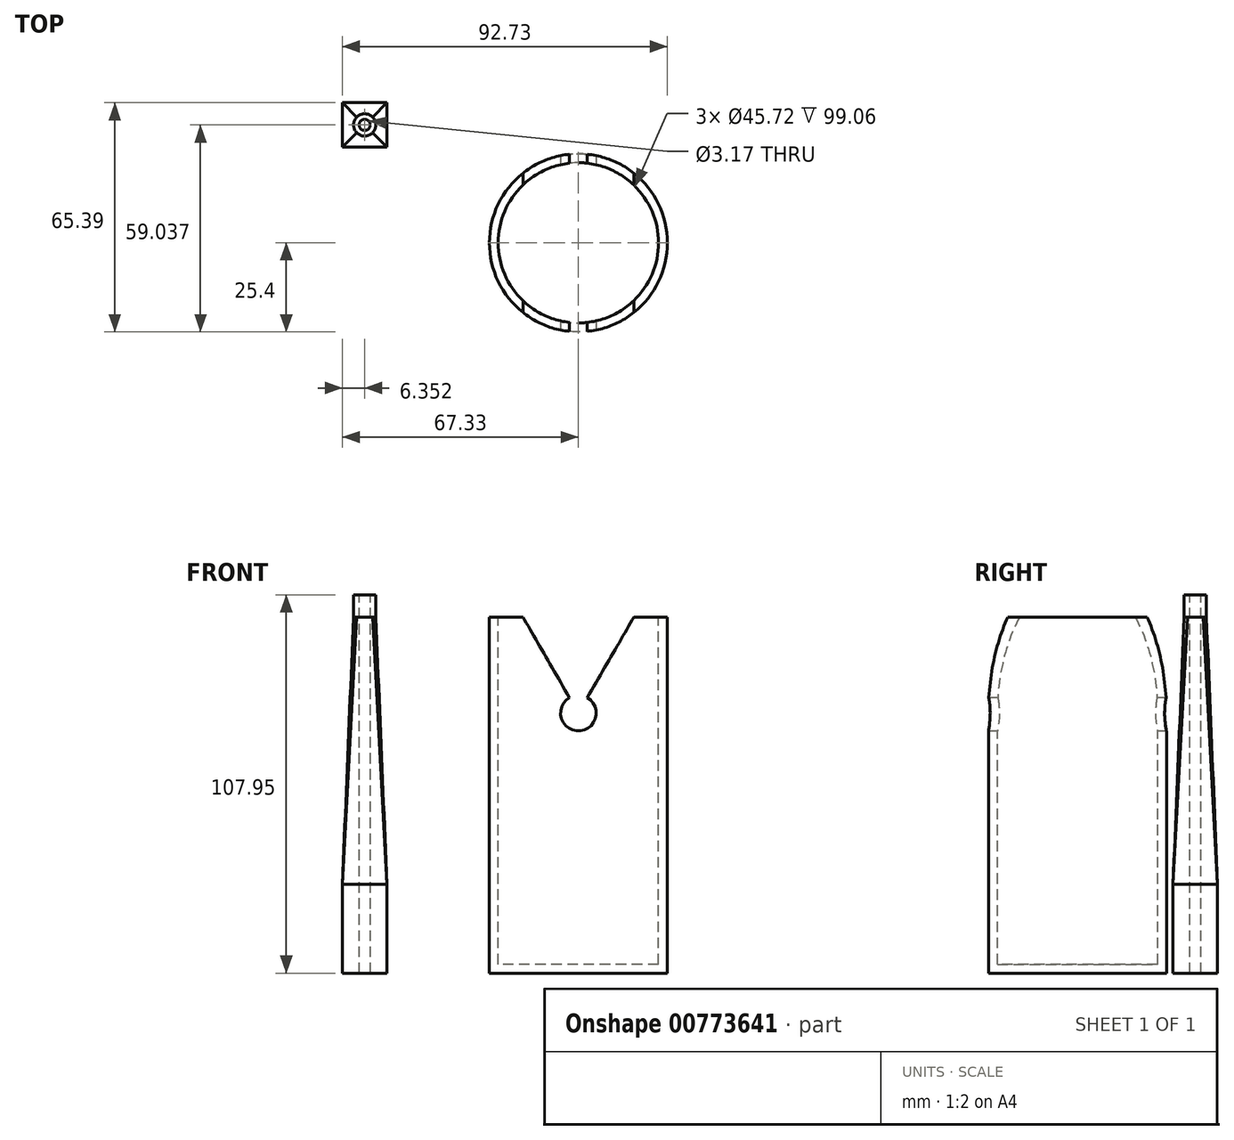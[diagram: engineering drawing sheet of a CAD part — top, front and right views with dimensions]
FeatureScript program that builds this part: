
annotation { "Feature Type Name" : "Feature", "Feature Type Description" : "" }
export const myFeature = defineFeature(function(context is Context, id is Id, definition is map)
    precondition{}
    {
        {
            var Q0;
            Q0=qCreatedBy(makeId("Top.planeOp"),FACE);
            var sketch = newSketch(context, id + "F0", { "sketchPlane" : qUnion([Q0])});
            skCircle(sketch, "E0", {"center": v(0, 0) * mm, "radius": 25.4 * mm});
            skLineSegment(sketch, "E1.bottom", {"start": v(-67.33, 39.99) * mm, "end": v(-54.63, 39.99) * mm});
            skLineSegment(sketch, "E1.top", {"start": v(-67.33, 27.29) * mm, "end": v(-54.63, 27.29) * mm});
            skLineSegment(sketch, "E1.left", {"start": v(-67.33, 39.99) * mm, "end": v(-67.33, 27.29) * mm});
            skLineSegment(sketch, "E1.right", {"start": v(-54.63, 39.99) * mm, "end": v(-54.63, 27.29) * mm});
            skSolve(sketch);
        }
        {
            var Q0;
            Q0=makeQuery(id+"F0.imprint","IMPRINT",FACE,{"disambiguationData":[TD([[makeQuery(id+"F0.imprint","IMPRINT",EDGE,{"derivedFrom":sQuery(id+"F0.wireOp",EDGE,"E0")}),1.0]])]});
            extrude(context, id + "F1", {"entities" : qUnion([Q0]), "depth" : 101.6 * mm, "offsetDistance" : 25.4 * mm});
        }
        {
            var Q0;
            Q0=makeQuery(id+"F1.opExtrude","CAP_FACE",FACE,{"disambiguationData":[OSD([sQuery(id+"F0.wireOp",EDGE,"E0")])],"isStart":false});
            var sketch = newSketch(context, id + "F2", { "sketchPlane" : qUnion([Q0])});
            skCircle(sketch, "E2", {"center": v(0, 0) * mm, "radius": 22.86 * mm});
            skSolve(sketch);
        }
        {
            var Q0;
            Q0=makeQuery(id+"F2.imprint","IMPRINT",FACE,{"disambiguationData":[TD([[makeQuery(id+"F2.imprint","IMPRINT",EDGE,{"derivedFrom":sQuery(id+"F2.wireOp",EDGE,"E2")}),1.0]])]});
            extrude(context, id + "F3", {"entities" : qUnion([Q0]), "operationType" : NewBodyOperationType.REMOVE, "oppositeDirection" : true, "depth" : 99.06 * mm, "offsetDistance" : 25.4 * mm});
        }
        {
            var Q0;
            Q0=qCreatedBy(makeId("Front.planeOp"),FACE);
            cPlane(context, id + "F4", {"entities" : qUnion([Q0]), "cplaneType" : CPlaneType.OFFSET, "offset" : 25.4 * mm, "width" : 152.4 * mm, "height" : 152.4 * mm});
        }
        {
            var Q0;
            Q0=qCreatedBy(id+"F4.planeOp",FACE);
            var sketch = newSketch(context, id + "F5", { "sketchPlane" : qUnion([Q0])});
            skLineSegment(sketch, "E3", {"start": v(-17.14, 103.86) * mm, "end": v(0, 74.16) * mm});
            skLineSegment(sketch, "E4", {"start": v(0, 74.16) * mm, "end": v(17.14, 103.86) * mm});
            skLineSegment(sketch, "E5", {"start": v(17.14, 103.86) * mm, "end": v(-17.14, 103.86) * mm});
            skCircle(sketch, "E6", {"center": v(0, 74.16) * mm, "radius": 5.08 * mm});
            skSolve(sketch);
        }
        {
            var Q0;
            Q0=makeQuery(id+"F5.imprint","IMPRINT",FACE,{"disambiguationData":[TD([[makeQuery(id+"F5.imprint","IMPRINT",EDGE,{"derivedFrom":sQuery(id+"F5.wireOp",EDGE,"E3")}),1.0]])]});
            var Q1;
            {var subQ0=sQuery(id+"F5.wireOp",EDGE,"E5");Q1=makeQuery(id+"F5.imprint","IMPRINT",FACE,{"disambiguationData":[TD([[makeQuery(id+"F5.imprint","IMPRINT",EDGE,{"derivedFrom":subQ0}),1.0]])]});}
            var Q2;
            {var subQ0=sQuery(id+"F5.wireOp",EDGE,"E4");var subQ1=sQuery(id+"F5.wireOp",EDGE,"E3");var subQ2=makeQuery(id+"F5.imprint","INTERSECT",VERTEX,{"derivedFrom":[subQ1,subQ0]});Q2=makeQuery(id+"F5.imprint","IMPRINT",FACE,{"disambiguationData":[TD([[makeQuery(id+"F5.imprint","IMPRINT",EDGE,{"disambiguationData":[TD([[subQ2,1.0]])],"derivedFrom":subQ1}),-1.0]])]});}
            extrude(context, id + "F6", {"entities" : qUnion([Q0, Q1, Q2]), "operationType" : NewBodyOperationType.REMOVE, "oppositeDirection" : true, "depth" : 50.8 * mm, "offsetDistance" : 25.4 * mm});
        }
        {
            var Q0;
            Q0=makeQuery(id+"F0.imprint","IMPRINT",FACE,{"disambiguationData":[TD([[makeQuery(id+"F0.imprint","IMPRINT",EDGE,{"derivedFrom":sQuery(id+"F0.wireOp",EDGE,"E1.bottom")}),-1.0]])]});
            extrude(context, id + "F7", {"entities" : qUnion([Q0]), "depth" : 25.4 * mm, "offsetDistance" : 25.4 * mm});
        }
        {
            var Q0;
            {var subQ0=sQuery(id+"F0.wireOp",EDGE,"E0");Q0=makeQuery(id+"F6.boolean.opBoolean","SPLIT",FACE,{"disambiguationData":[TD([makeQuery(id+"F6.opExtrude","SWEPT_FACE",FACE,{"disambiguationData":[OSD([sQuery(id+"F5.wireOp",EDGE,"E3")])]})])],"derivedFrom":makeQuery(id+"F1.opExtrude","CAP_FACE",FACE,{"disambiguationData":[OSD([subQ0])],"isStart":false})});}
            var sketch = newSketch(context, id + "F8", { "sketchPlane" : qUnion([Q0])});
            skCircle(sketch, "E7", {"center": v(-60.98, 33.64) * mm, "radius": 3.18 * mm});
            skSolve(sketch);
        }
        {
            var Q0;
            Q0=makeQuery(id+"F8.imprint","IMPRINT",FACE,{"disambiguationData":[TD([[makeQuery(id+"F8.imprint","IMPRINT",EDGE,{"derivedFrom":sQuery(id+"F8.wireOp",EDGE,"E7")}),1.0]])]});
            extrude(context, id + "F9", {"entities" : qUnion([Q0]), "depth" : 6.35 * mm, "offsetDistance" : 25.4 * mm});
        }
        {
            var Q1;
            Q1=makeQuery(id+"F9.opExtrude","CAP_FACE",FACE,{"disambiguationData":[OSD([sQuery(id+"F8.wireOp",EDGE,"E7")])],"isStart":true});
            var Q2;
            Q2=makeQuery(id+"F7.opExtrude","CAP_FACE",FACE,{"disambiguationData":[OSD([sQuery(id+"F0.wireOp",EDGE,"E1.bottom"),sQuery(id+"F0.wireOp",EDGE,"E1.top"),sQuery(id+"F0.wireOp",EDGE,"E1.left"),sQuery(id+"F0.wireOp",EDGE,"E1.right")])],"isStart":false});
            loft(context, id + "F10", {"operationType" : NewBodyOperationType.ADD, "sheetProfilesArray" : [{ "sheetProfileEntities" : qUnion([Q1]) }, { "sheetProfileEntities" : qUnion([Q2]) }]});
        }
        {
            var Q0;
            Q0=makeQuery(id+"F9.opExtrude","CAP_FACE",FACE,{"disambiguationData":[OSD([sQuery(id+"F8.wireOp",EDGE,"E7")])],"isStart":false});
            var sketch = newSketch(context, id + "F11", { "sketchPlane" : qUnion([Q0])});
            skCircle(sketch, "E8", {"center": v(-60.98, 33.64) * mm, "radius": 1.59 * mm});
            skSolve(sketch);
        }
        {
            var Q0;
            Q0=makeQuery(id+"F11.imprint","IMPRINT",FACE,{"disambiguationData":[TD([[makeQuery(id+"F11.imprint","IMPRINT",EDGE,{"derivedFrom":sQuery(id+"F11.wireOp",EDGE,"E8")}),1.0]])]});
            extrude(context, id + "F12", {"entities" : qUnion([Q0]), "operationType" : NewBodyOperationType.REMOVE, "oppositeDirection" : true, "depth" : 130.05 * mm, "offsetDistance" : 25.4 * mm});
        }
    });
